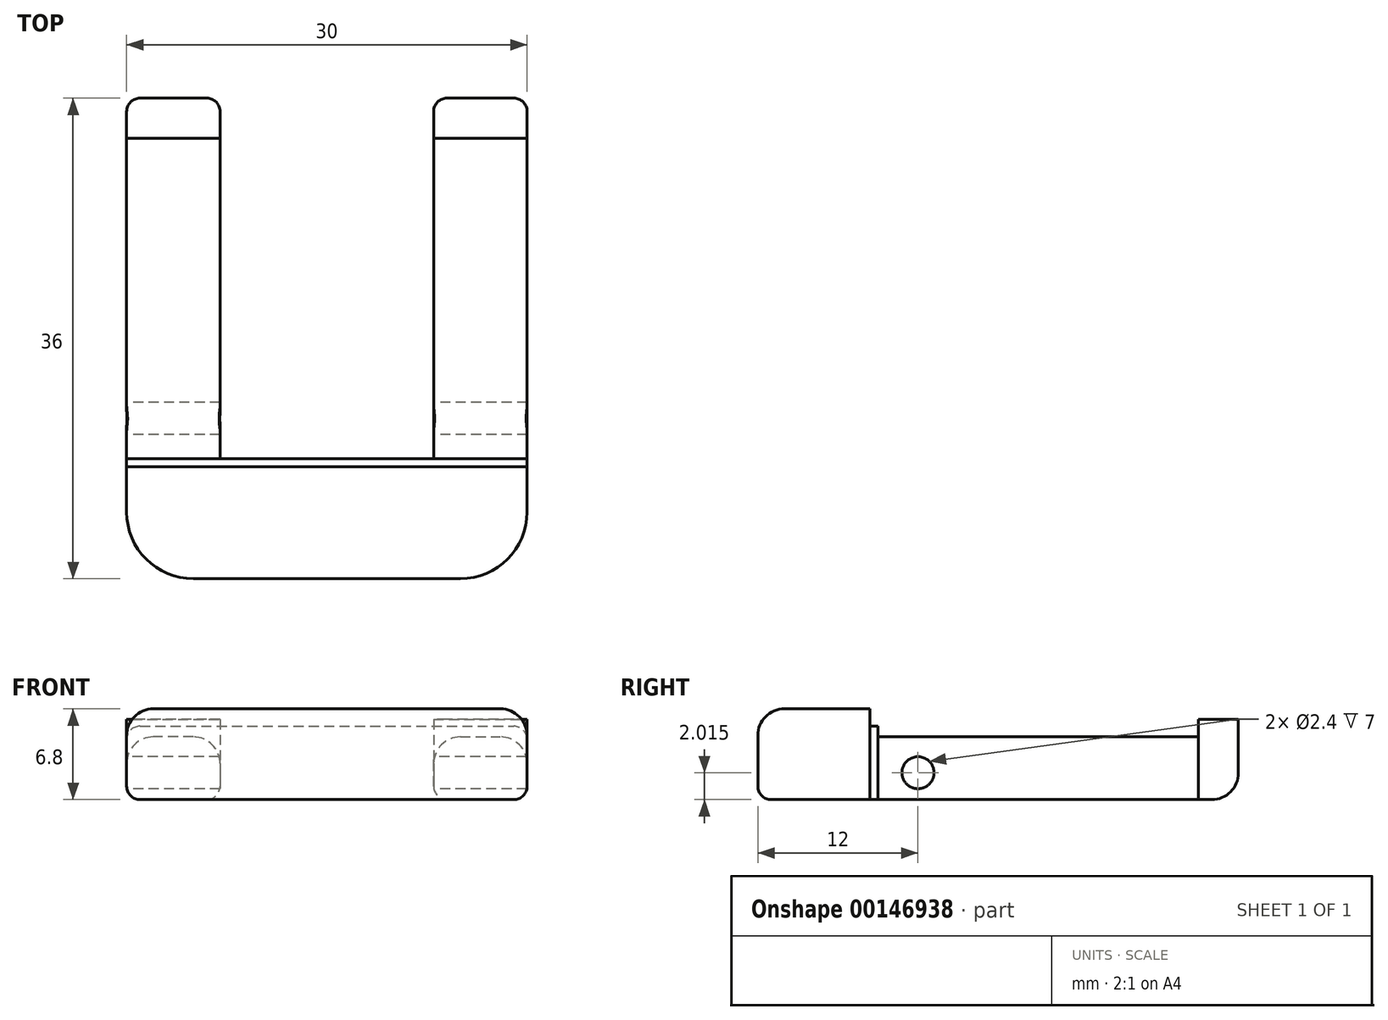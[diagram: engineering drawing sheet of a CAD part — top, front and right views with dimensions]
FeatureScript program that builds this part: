
annotation { "Feature Type Name" : "Feature", "Feature Type Description" : "" }
export const myFeature = defineFeature(function(context is Context, id is Id, definition is map)
    precondition{}
    {
        {
            var Q0;
            Q0=qCreatedBy(makeId("Top.planeOp"),FACE);
            var sketch = newSketch(context, id + "F0", { "sketchPlane" : qUnion([Q0])});
            skLineSegment(sketch, "E0", {"start": v(-15, 33) * mm, "end": v(-8, 33) * mm});
            skLineSegment(sketch, "E1", {"start": v(15, 33) * mm, "end": v(15, 0) * mm});
            skLineSegment(sketch, "E2", {"start": v(15, 0) * mm, "end": v(-15, 0) * mm});
            skLineSegment(sketch, "E3", {"start": v(-15, 0) * mm, "end": v(-15, 33) * mm});
            skLineSegment(sketch, "E4", {"start": v(-8, 33) * mm, "end": v(-8, 9) * mm});
            skLineSegment(sketch, "E5", {"start": v(8, 9) * mm, "end": v(8, 33) * mm});
            skLineSegment(sketch, "E6", {"start": v(-8, 9) * mm, "end": v(8, 9) * mm});
            skLineSegment(sketch, "E7.trimOffspring", {"start": v(8, 33) * mm, "end": v(15, 33) * mm});
            skLineSegment(sketch, "E8", {"start": v(-15, 33) * mm, "end": v(-15, 36) * mm});
            skLineSegment(sketch, "E9", {"start": v(-8, 33) * mm, "end": v(-8, 36) * mm});
            skLineSegment(sketch, "E10", {"start": v(-8, 36) * mm, "end": v(-15, 36) * mm});
            skLineSegment(sketch, "E11", {"start": v(8, 33) * mm, "end": v(8, 36) * mm});
            skLineSegment(sketch, "E12", {"start": v(15, 33) * mm, "end": v(15, 36) * mm});
            skLineSegment(sketch, "E13", {"start": v(15, 36) * mm, "end": v(8, 36) * mm});
            skLineSegment(sketch, "E14", {"start": v(8, 9) * mm, "end": v(15, 9) * mm});
            skLineSegment(sketch, "E15", {"start": v(-8, 9) * mm, "end": v(-15, 9) * mm});
            skLineSegment(sketch, "E16", {"start": v(-15, 8.4) * mm, "end": v(15, 8.4) * mm});
            skSolve(sketch);
        }
        {
            var Q0;
            {var subQ0=sQuery(id+"F0.wireOp",EDGE,"E2");Q0=makeQuery(id+"F0.imprint","IMPRINT",FACE,{"disambiguationData":[TD([[makeQuery(id+"F0.imprint","IMPRINT",EDGE,{"derivedFrom":subQ0}),-1.0]])]});}
            extrude(context, id + "F1", {"entities" : qUnion([Q0]), "depth" : 6.8 * mm});
        }
        {
            var Q0;
            {var subQ0=sQuery(id+"F0.wireOp",EDGE,"E0");Q0=makeQuery(id+"F0.imprint","IMPRINT",FACE,{"disambiguationData":[TD([[makeQuery(id+"F0.imprint","IMPRINT",EDGE,{"derivedFrom":subQ0}),-1.0]])]});}
            var Q1;
            Q1=makeQuery(id+"F0.imprint","IMPRINT",FACE,{"disambiguationData":[TD([[makeQuery(id+"F0.imprint","IMPRINT",EDGE,{"derivedFrom":sQuery(id+"F0.wireOp",EDGE,"E5")}),-1.0]])]});
            extrude(context, id + "F2", {"entities" : qUnion([Q0, Q1]), "depth" : 4.7 * mm});
        }
        {
            var Q0;
            Q0=makeQuery(id+"F0.imprint","IMPRINT",FACE,{"disambiguationData":[TD([[makeQuery(id+"F0.imprint","IMPRINT",EDGE,{"derivedFrom":sQuery(id+"F0.wireOp",EDGE,"E0")}),1.0]])]});
            var Q1;
            Q1=makeQuery(id+"F0.imprint","IMPRINT",FACE,{"disambiguationData":[TD([[makeQuery(id+"F0.imprint","IMPRINT",EDGE,{"derivedFrom":sQuery(id+"F0.wireOp",EDGE,"E7.trimOffspring")}),1.0]])]});
            extrude(context, id + "F3", {"entities" : qUnion([Q0, Q1]), "depth" : 6 * mm});
        }
        {
            var Q0;
            Q0=makeQuery(id+"F0.imprint","IMPRINT",FACE,{"disambiguationData":[TD([[makeQuery(id+"F0.imprint","IMPRINT",EDGE,{"derivedFrom":sQuery(id+"F0.wireOp",EDGE,"E6")}),-1.0]])]});
            extrude(context, id + "F4", {"entities" : qUnion([Q0]), "depth" : 5.5 * mm});
        }
        {
            var Q0;
            Q0=makeQuery(id+"F3.opExtrude","CAP_EDGE",EDGE,{"disambiguationData":[OSD([sQuery(id+"F0.wireOp",EDGE,"E13")])],"isStart":true});
            var Q1;
            Q1=makeQuery(id+"F3.opExtrude","CAP_EDGE",EDGE,{"disambiguationData":[OSD([sQuery(id+"F0.wireOp",EDGE,"E10")])],"isStart":true});
            var Q2;
            Q2=makeQuery(id+"F1.opExtrude","CAP_EDGE",EDGE,{"disambiguationData":[OSD([sQuery(id+"F0.wireOp",EDGE,"E1")])],"isStart":false});
            var Q3;
            Q3=makeQuery(id+"F1.opExtrude","CAP_EDGE",EDGE,{"disambiguationData":[OSD([sQuery(id+"F0.wireOp",EDGE,"E3")])],"isStart":false});
            var Q4;
            Q4=makeQuery(id+"F2.opExtrude","CAP_EDGE",EDGE,{"disambiguationData":[OSD([sQuery(id+"F0.wireOp",EDGE,"E3")])],"isStart":false});
            var Q5;
            Q5=makeQuery(id+"F2.opExtrude","CAP_EDGE",EDGE,{"disambiguationData":[OSD([sQuery(id+"F0.wireOp",EDGE,"E4")])],"isStart":false});
            var Q6;
            Q6=makeQuery(id+"F2.opExtrude","CAP_EDGE",EDGE,{"disambiguationData":[OSD([sQuery(id+"F0.wireOp",EDGE,"E5")])],"isStart":false});
            var Q7;
            Q7=makeQuery(id+"F2.opExtrude","CAP_EDGE",EDGE,{"disambiguationData":[OSD([sQuery(id+"F0.wireOp",EDGE,"E1")])],"isStart":false});
            var Q8;
            Q8=makeQuery(id+"F1.opExtrude","CAP_EDGE",EDGE,{"disambiguationData":[OSD([sQuery(id+"F0.wireOp",EDGE,"E2")])],"isStart":false});
            fillet(context, id + "F5", {"entities" : qUnion([Q0, Q1, Q2, Q3, Q4, Q5, Q6, Q7, Q8]), "radius" : 2 * mm, "tangentPropagation" : true, "allowEdgeOverflow" : false});
        }
        {
            var Q0;
            Q0=makeQuery(id+"F4.opExtrude","CAP_EDGE",EDGE,{"disambiguationData":[OSD([sQuery(id+"F0.wireOp",EDGE,"E1")])],"isStart":false});
            var Q1;
            Q1=makeQuery(id+"F4.opExtrude","CAP_EDGE",EDGE,{"disambiguationData":[OSD([sQuery(id+"F0.wireOp",EDGE,"E3")])],"isStart":false});
            fillet(context, id + "F6", {"entities" : qUnion([Q0, Q1]), "radius" : 1 * mm, "tangentPropagation" : true, "allowEdgeOverflow" : false});
        }
        {
            var Q0;
            Q0=makeQuery(id+"F3.opExtrude","CAP_EDGE",EDGE,{"disambiguationData":[OSD([sQuery(id+"F0.wireOp",EDGE,"E12")])],"isStart":true});
            var Q1;
            Q1=makeQuery(id+"F5.opFillet","BLEND_EDGE",EDGE,{"blendedFrom":[makeQuery(id+"F3.opExtrude","CAP_EDGE",EDGE,{"disambiguationData":[OSD([sQuery(id+"F0.wireOp",EDGE,"E13")])],"isStart":true}),makeQuery(id+"F3.opExtrude","SWEPT_FACE",FACE,{"disambiguationData":[OSD([sQuery(id+"F0.wireOp",EDGE,"E12")])]})],"blendedInto":[makeQuery(id+"F3.opExtrude","SWEPT_FACE",FACE,{"disambiguationData":[OSD([sQuery(id+"F0.wireOp",EDGE,"E12")])]})]});
            var Q2;
            Q2=makeQuery(id+"F2.opExtrude","CAP_EDGE",EDGE,{"disambiguationData":[OSD([sQuery(id+"F0.wireOp",EDGE,"E1")])],"isStart":true});
            var Q3;
            Q3=makeQuery(id+"F4.opExtrude","CAP_EDGE",EDGE,{"disambiguationData":[OSD([sQuery(id+"F0.wireOp",EDGE,"E1")])],"isStart":true});
            var Q4;
            Q4=makeQuery(id+"F1.opExtrude","CAP_EDGE",EDGE,{"disambiguationData":[OSD([sQuery(id+"F0.wireOp",EDGE,"E1")])],"isStart":true});
            var Q5;
            Q5=makeQuery(id+"F1.opExtrude","CAP_EDGE",EDGE,{"disambiguationData":[OSD([sQuery(id+"F0.wireOp",EDGE,"E2")])],"isStart":true});
            var Q6;
            Q6=makeQuery(id+"F1.opExtrude","CAP_EDGE",EDGE,{"disambiguationData":[OSD([sQuery(id+"F0.wireOp",EDGE,"E3")])],"isStart":true});
            var Q7;
            Q7=makeQuery(id+"F2.opExtrude","CAP_EDGE",EDGE,{"disambiguationData":[OSD([sQuery(id+"F0.wireOp",EDGE,"E5")])],"isStart":true});
            var Q8;
            Q8=makeQuery(id+"F2.opExtrude","CAP_EDGE",EDGE,{"disambiguationData":[OSD([sQuery(id+"F0.wireOp",EDGE,"E4")])],"isStart":true});
            var Q9;
            Q9=makeQuery(id+"F2.opExtrude","CAP_EDGE",EDGE,{"disambiguationData":[OSD([sQuery(id+"F0.wireOp",EDGE,"E3")])],"isStart":true});
            var Q10;
            Q10=makeQuery(id+"F3.opExtrude","CAP_EDGE",EDGE,{"disambiguationData":[OSD([sQuery(id+"F0.wireOp",EDGE,"E8")])],"isStart":true});
            var Q11;
            Q11=makeQuery(id+"F5.opFillet","BLEND_EDGE",EDGE,{"blendedFrom":[makeQuery(id+"F3.opExtrude","CAP_EDGE",EDGE,{"disambiguationData":[OSD([sQuery(id+"F0.wireOp",EDGE,"E10")])],"isStart":true}),makeQuery(id+"F3.opExtrude","SWEPT_FACE",FACE,{"disambiguationData":[OSD([sQuery(id+"F0.wireOp",EDGE,"E8")])]})],"blendedInto":[makeQuery(id+"F3.opExtrude","SWEPT_FACE",FACE,{"disambiguationData":[OSD([sQuery(id+"F0.wireOp",EDGE,"E8")])]})]});
            var Q12;
            Q12=makeQuery(id+"F3.opExtrude","CAP_EDGE",EDGE,{"disambiguationData":[OSD([sQuery(id+"F0.wireOp",EDGE,"E9")])],"isStart":true});
            var Q13;
            Q13=makeQuery(id+"F5.opFillet","BLEND_EDGE",EDGE,{"blendedFrom":[makeQuery(id+"F3.opExtrude","CAP_EDGE",EDGE,{"disambiguationData":[OSD([sQuery(id+"F0.wireOp",EDGE,"E10")])],"isStart":true}),makeQuery(id+"F3.opExtrude","SWEPT_FACE",FACE,{"disambiguationData":[OSD([sQuery(id+"F0.wireOp",EDGE,"E9")])]})],"blendedInto":[makeQuery(id+"F3.opExtrude","SWEPT_FACE",FACE,{"disambiguationData":[OSD([sQuery(id+"F0.wireOp",EDGE,"E9")])]})]});
            var Q14;
            Q14=makeQuery(id+"F3.opExtrude","CAP_EDGE",EDGE,{"disambiguationData":[OSD([sQuery(id+"F0.wireOp",EDGE,"E11")])],"isStart":true});
            var Q15;
            Q15=makeQuery(id+"F5.opFillet","BLEND_EDGE",EDGE,{"blendedFrom":[makeQuery(id+"F3.opExtrude","CAP_EDGE",EDGE,{"disambiguationData":[OSD([sQuery(id+"F0.wireOp",EDGE,"E13")])],"isStart":true}),makeQuery(id+"F3.opExtrude","SWEPT_FACE",FACE,{"disambiguationData":[OSD([sQuery(id+"F0.wireOp",EDGE,"E11")])]})],"blendedInto":[makeQuery(id+"F3.opExtrude","SWEPT_FACE",FACE,{"disambiguationData":[OSD([sQuery(id+"F0.wireOp",EDGE,"E11")])]})]});
            var Q16;
            Q16=makeQuery(id+"F3.opExtrude","SWEPT_EDGE",EDGE,{"disambiguationData":[OSD([sQuery(id+"F0.wireOp",EDGE,"E8"),sQuery(id+"F0.wireOp",EDGE,"E10")])]});
            var Q17;
            Q17=makeQuery(id+"F3.opExtrude","SWEPT_EDGE",EDGE,{"disambiguationData":[OSD([sQuery(id+"F0.wireOp",EDGE,"E9"),sQuery(id+"F0.wireOp",EDGE,"E10")])]});
            var Q18;
            Q18=makeQuery(id+"F3.opExtrude","SWEPT_EDGE",EDGE,{"disambiguationData":[OSD([sQuery(id+"F0.wireOp",EDGE,"E11"),sQuery(id+"F0.wireOp",EDGE,"E13")])]});
            var Q19;
            Q19=makeQuery(id+"F3.opExtrude","SWEPT_EDGE",EDGE,{"disambiguationData":[OSD([sQuery(id+"F0.wireOp",EDGE,"E12"),sQuery(id+"F0.wireOp",EDGE,"E13")])]});
            var Q20;
            Q20=makeQuery(id+"F4.opExtrude","CAP_EDGE",EDGE,{"disambiguationData":[OSD([sQuery(id+"F0.wireOp",EDGE,"E3")])],"isStart":true});
            fillet(context, id + "F7", {"entities" : qUnion([Q0, Q1, Q2, Q3, Q4, Q5, Q6, Q7, Q8, Q9, Q10, Q11, Q12, Q13, Q14, Q15, Q16, Q17, Q18, Q19, Q20]), "radius" : 1 * mm, "tangentPropagation" : true, "allowEdgeOverflow" : false});
        }
        {
            var Q0;
            Q0=makeQuery(id+"F1.opExtrude","SWEPT_EDGE",EDGE,{"disambiguationData":[OSD([sQuery(id+"F0.wireOp",EDGE,"E1"),sQuery(id+"F0.wireOp",EDGE,"E2")])]});
            var Q1;
            Q1=makeQuery(id+"F1.opExtrude","SWEPT_EDGE",EDGE,{"disambiguationData":[OSD([sQuery(id+"F0.wireOp",EDGE,"E2"),sQuery(id+"F0.wireOp",EDGE,"E3")])]});
            fillet(context, id + "F8", {"entities" : qUnion([Q0, Q1]), "radius" : 5 * mm, "tangentPropagation" : true, "allowEdgeOverflow" : false});
        }
        {
            var Q0;
            Q0=qCreatedBy(makeId("Right.planeOp"),FACE);
            var sketch = newSketch(context, id + "F9", { "sketchPlane" : qUnion([Q0])});
            skCircle(sketch, "E17", {"center": v(12, 2.01) * mm, "radius": 1.2 * mm});
            skSolve(sketch);
        }
        {
            var Q0;
            Q0 = qSketchRegion(id + "F9", true);
            extrude(context, id + "F10", {"entities" : qUnion([Q0]), "operationType" : NewBodyOperationType.REMOVE, "endBound" : BoundingType.SYMMETRIC, "depth" : 111 * mm});
        }
    });
